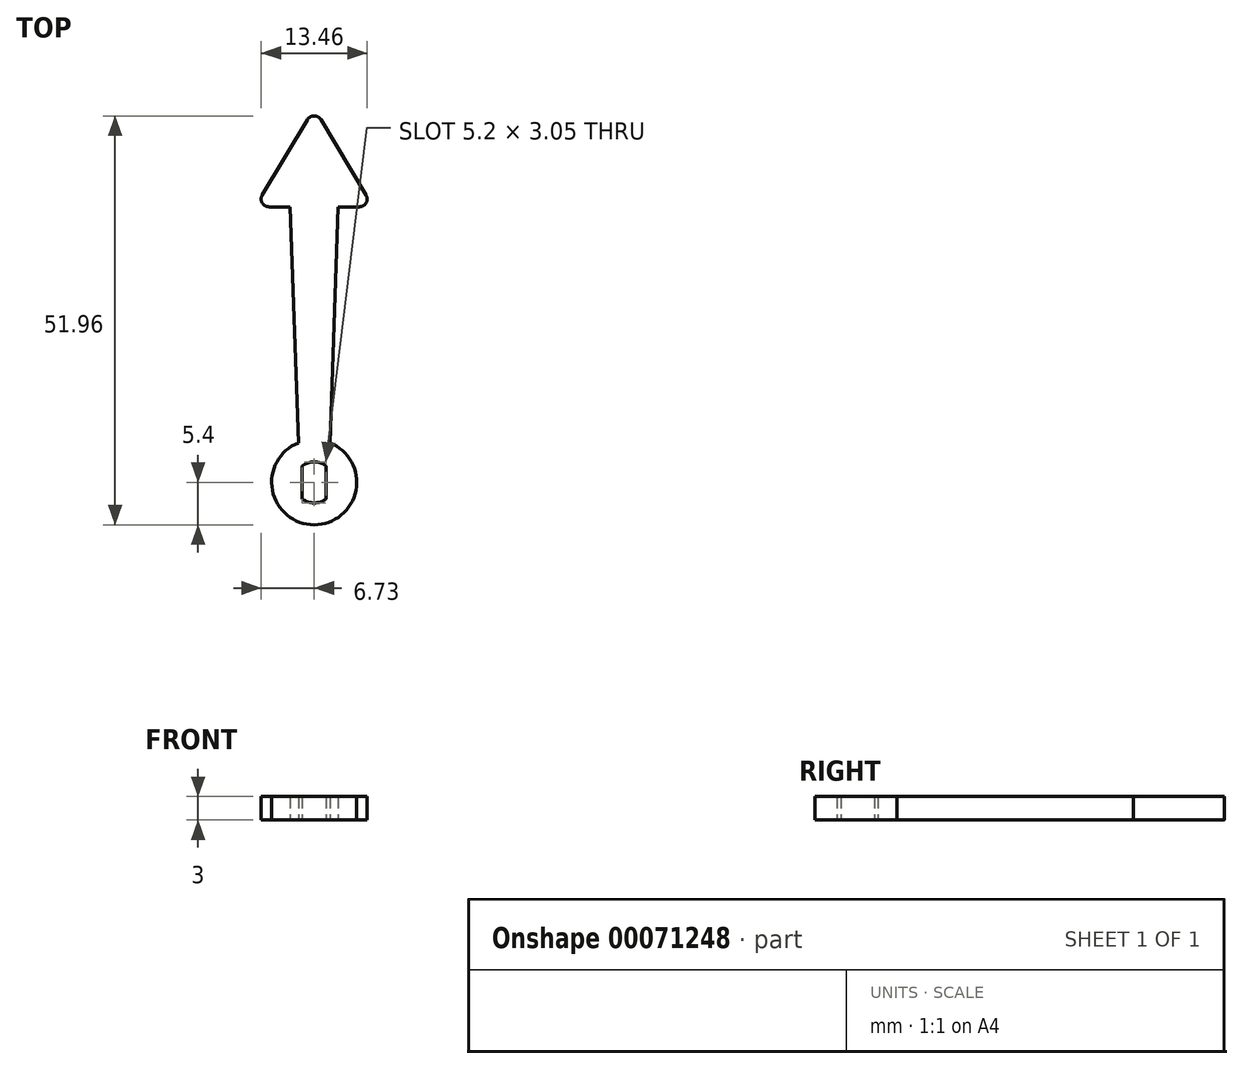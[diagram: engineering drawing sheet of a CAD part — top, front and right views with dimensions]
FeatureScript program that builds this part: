
annotation { "Feature Type Name" : "Feature", "Feature Type Description" : "" }
export const myFeature = defineFeature(function(context is Context, id is Id, definition is map)
    precondition{}
    {
        {
            var Q0;
            Q0=qCreatedBy(makeId("Top.planeOp"),FACE);
            var sketch = newSketch(context, id + "F0", { "sketchPlane" : qUnion([Q0])});
            skCircle(sketch, "E0", {"center": v(0, 0) * mm, "radius": 2.6 * mm});
            skCircle(sketch, "E1", {"center": v(0, 0) * mm, "radius": 5.4 * mm});
            skLineSegment(sketch, "E2", {"start": v(-1.53, 2.1) * mm, "end": v(-1.53, -2.1) * mm});
            skLineSegment(sketch, "E3", {"start": v(1.52, -2.1) * mm, "end": v(1.52, 2.1) * mm});
            skSolve(sketch);
        }
        {
            var Q0;
            Q0=makeQuery(id+"F0.imprint","IMPRINT",FACE,{"disambiguationData":[TD([[makeQuery(id+"F0.imprint","IMPRINT",EDGE,{"derivedFrom":sQuery(id+"F0.wireOp",EDGE,"E1")}),1.0]])]});
            var Q1;
            {var subQ0=sQuery(id+"F0.wireOp",EDGE,"E3");Q1=makeQuery(id+"F0.imprint","IMPRINT",FACE,{"disambiguationData":[TD([[makeQuery(id+"F0.imprint","IMPRINT",EDGE,{"derivedFrom":subQ0}),-1.0]])]});}
            var Q2;
            {var subQ0=sQuery(id+"F0.wireOp",EDGE,"E2");Q2=makeQuery(id+"F0.imprint","IMPRINT",FACE,{"disambiguationData":[TD([[makeQuery(id+"F0.imprint","IMPRINT",EDGE,{"derivedFrom":subQ0}),-1.0]])]});}
            extrude(context, id + "F1", {"entities" : qUnion([Q0, Q1, Q2]), "endBound" : BoundingType.SYMMETRIC, "depth" : 3 * mm});
        }
        {
            var Q0;
            Q0=qCreatedBy(makeId("Top.planeOp"),FACE);
            var sketch = newSketch(context, id + "F2", { "sketchPlane" : qUnion([Q0])});
            skLineSegment(sketch, "E4", {"start": v(0, 0) * mm, "end": v(0, 35) * mm, "construction": true});
            skLineSegment(sketch, "E5", {"start": v(0, 5.02) * mm, "end": v(2, 5.02) * mm});
            skLineSegment(sketch, "E6", {"start": v(2, 5.02) * mm, "end": v(3.05, 35) * mm});
            skLineSegment(sketch, "E7", {"start": v(3.05, 35) * mm, "end": v(0, 35) * mm});
            skCircle(sketch, "E8", {"center": v(0, 0) * mm, "radius": 5.4 * mm, "construction": true});
            skLineSegment(sketch, "E9.MirrorCS", {"start": v(-3.05, 35) * mm, "end": v(0, 35) * mm});
            skLineSegment(sketch, "E10.MirrorCS", {"start": v(-2, 5.02) * mm, "end": v(-3.05, 35) * mm});
            skLineSegment(sketch, "E11.MirrorCS", {"start": v(0, 5.02) * mm, "end": v(-2, 5.02) * mm});
            skSolve(sketch);
        }
        {
            var Q0;
            Q0=makeQuery(id+"F2.imprint","IMPRINT",FACE,{"disambiguationData":[TD([[makeQuery(id+"F2.imprint","IMPRINT",EDGE,{"derivedFrom":sQuery(id+"F2.wireOp",EDGE,"E5")}),1.0]])]});
            extrude(context, id + "F3", {"entities" : qUnion([Q0]), "operationType" : NewBodyOperationType.ADD, "endBound" : BoundingType.SYMMETRIC, "depth" : 3 * mm});
        }
        {
            var Q0;
            Q0=makeQuery(id+"F3.boolean.opBoolean","MERGE",FACE,{"derivedFrom":[makeQuery(id+"F1.opExtrude","CAP_FACE",FACE,{"disambiguationData":[OSD([sQuery(id+"F0.wireOp",EDGE,"E0"),sQuery(id+"F0.wireOp",EDGE,"E1"),sQuery(id+"F0.wireOp",EDGE,"E2"),sQuery(id+"F0.wireOp",EDGE,"E3")])],"isStart":false}),makeQuery(id+"F3.opExtrude","CAP_FACE",FACE,{"disambiguationData":[OSD([sQuery(id+"F2.wireOp",EDGE,"E5"),sQuery(id+"F2.wireOp",EDGE,"E6"),sQuery(id+"F2.wireOp",EDGE,"E7"),sQuery(id+"F2.wireOp",EDGE,"E9.MirrorCS"),sQuery(id+"F2.wireOp",EDGE,"E10.MirrorCS"),sQuery(id+"F2.wireOp",EDGE,"E11.MirrorCS")])],"isStart":false})]});
            var sketch = newSketch(context, id + "F4", { "sketchPlane" : qUnion([Q0])});
            skLineSegment(sketch, "E12", {"start": v(0, 35) * mm, "end": v(0, 47.5) * mm, "construction": true});
            skLineSegment(sketch, "E13", {"start": v(-7.5, 35) * mm, "end": v(7.5, 35) * mm});
            skLineSegment(sketch, "E14", {"start": v(-7.5, 35) * mm, "end": v(0, 47.5) * mm});
            skLineSegment(sketch, "E15", {"start": v(7.5, 35) * mm, "end": v(0, 47.5) * mm});
            skSolve(sketch);
        }
        {
            var Q0;
            Q0 = qSketchRegion(id + "F4", true);
            var Q1;
            Q1=makeQuery(id+"F3.boolean.opBoolean","MERGE",FACE,{"derivedFrom":[makeQuery(id+"F1.opExtrude","CAP_FACE",FACE,{"disambiguationData":[OSD([sQuery(id+"F0.wireOp",EDGE,"E0"),sQuery(id+"F0.wireOp",EDGE,"E1"),sQuery(id+"F0.wireOp",EDGE,"E2"),sQuery(id+"F0.wireOp",EDGE,"E3")])],"isStart":true}),makeQuery(id+"F3.opExtrude","CAP_FACE",FACE,{"disambiguationData":[OSD([sQuery(id+"F2.wireOp",EDGE,"E5"),sQuery(id+"F2.wireOp",EDGE,"E6"),sQuery(id+"F2.wireOp",EDGE,"E7"),sQuery(id+"F2.wireOp",EDGE,"E9.MirrorCS"),sQuery(id+"F2.wireOp",EDGE,"E10.MirrorCS"),sQuery(id+"F2.wireOp",EDGE,"E11.MirrorCS")])],"isStart":true})]});
            extrude(context, id + "F5", {"entities" : qUnion([Q0]), "operationType" : NewBodyOperationType.ADD, "endBound" : BoundingType.UP_TO_SURFACE, "oppositeDirection" : true, "endBoundEntityFace" : qUnion([Q1]), "depth" : 25 * mm});
        }
        {
            var Q0;
            Q0=makeQuery(id+"F5.opExtrude","SWEPT_EDGE",EDGE,{"disambiguationData":[OSD([sQuery(id+"F4.wireOp",EDGE,"E13"),sQuery(id+"F4.wireOp",EDGE,"E14")])]});
            var Q1;
            Q1=makeQuery(id+"F5.opExtrude","SWEPT_EDGE",EDGE,{"disambiguationData":[OSD([sQuery(id+"F4.wireOp",EDGE,"E14"),sQuery(id+"F4.wireOp",EDGE,"E15")])]});
            var Q2;
            Q2=makeQuery(id+"F5.opExtrude","SWEPT_EDGE",EDGE,{"disambiguationData":[OSD([sQuery(id+"F4.wireOp",EDGE,"E13"),sQuery(id+"F4.wireOp",EDGE,"E15")])]});
            fillet(context, id + "F6", {"entities" : qUnion([Q0, Q1, Q2]), "radius" : 1 * mm, "tangentPropagation" : true, "allowEdgeOverflow" : false});
        }
    });
